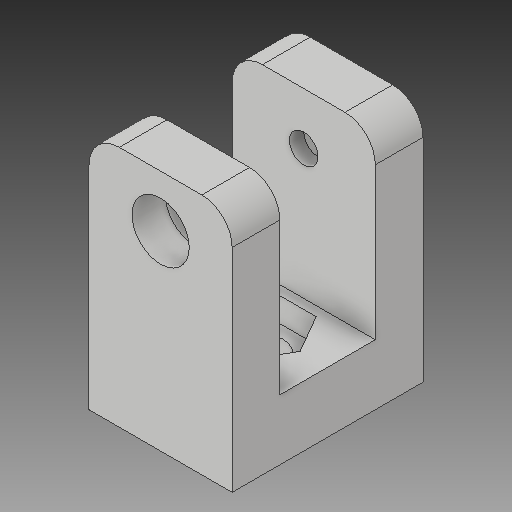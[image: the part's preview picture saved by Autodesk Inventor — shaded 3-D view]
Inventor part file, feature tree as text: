
AUTODESK INVENTOR PART (.ipt)
format: ipt  version: 2019 (Build 230136000, 136)  size: 198,656 bytes
history: native  units: in
note: dims shown in document units (in); Inventor stores cm internally (conversion verified against a paired STEP export)
features: extrude x9, sketch x9, projected_geometry x2, fillet x1
ambient origin geometry x8: Origin, YZ Plane, XZ Plane, XY Plane, X Axis, Y Axis, Z Axis, Center Point
bodies: Solid1 (feature_tree)
feature tree (21):
  extrude  "Extrusion1"  Depth=0.5906in
  extrude  "Extrusion2"  Depth=0.3937in
  extrude  "Extrusion3"  Depth=0.1181in
  fillet  "Fillet1"  Radius=0.75in
  extrude  "Extrusion4"  Depth=0.125in
  extrude  "Extrusion5"  Depth=0.315in
  extrude  "Extrusion6"  Depth=0.2362in
  extrude  "Extrusion7"  Depth=0.2205in
  extrude  "Extrusion8"  Depth=0.0394in TaperAngle=0.0deg
  extrude  "Extrusion9"  [1 undecoded]
  sketch  "Sketch1"  dims[d0=0.7087in d1=0.5906in]
  sketch  "Sketch2"  dims[d2=1.0in d3=0.0in d5=0.3937in]
  sketch  "Sketch3"  dims[d6=0.75in d7=0.0in d8=0.1181in d9=0.75in d10=0.0in]
  sketch  "Sketch4"  dims[d11=0.125in d12=0.2165in]
  sketch  "Sketch5"  dims[d13=0.75in d14=0.0in d15=0.315in]
  sketch  "Sketch6"  dims[d16=0.1in d17=0.0in d18=0.2362in]
  sketch  "Sketch7"  dims[d19=0.0984in d20=0.0in d21=0.2205in]
  sketch  "Sketch8"  dims[d22=0.0984in d23=0.0in d24=0.0394in d25=0.0in]
  projected_geometry  "Projected Loop1"
  sketch  "Sketch9"  dims[d26=0.0394in d27=0.0in]
  projected_geometry  "Projected Loop2"
note: 1 required parameter value undecoded (feature->parameter linkage not recoverable at this tier; creation-order binding heuristic only, values carry confidence <= 0.55)
